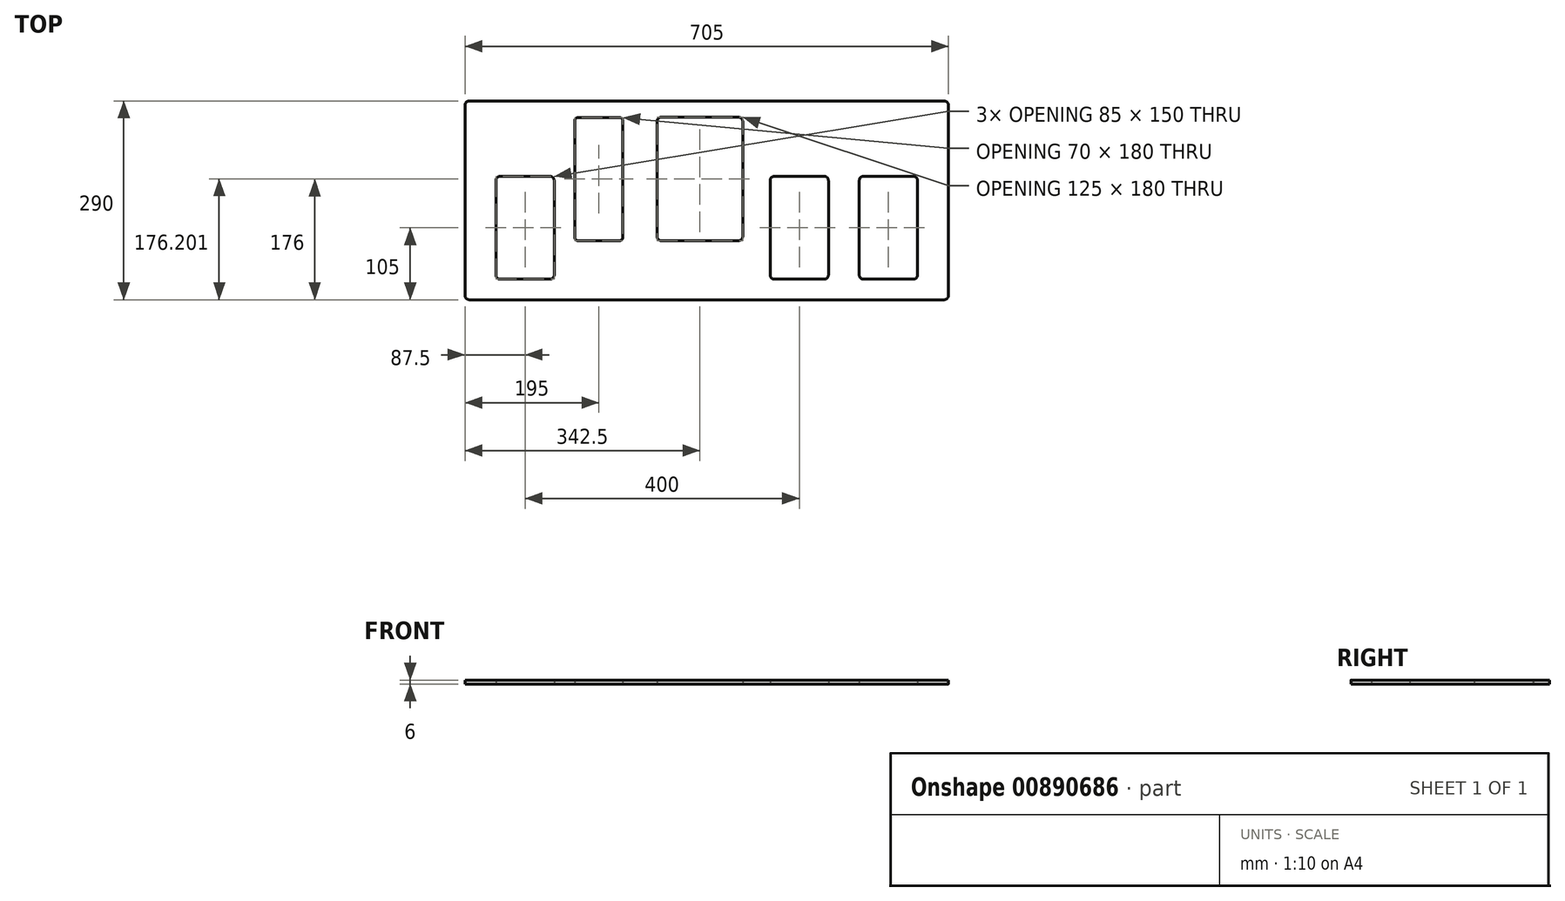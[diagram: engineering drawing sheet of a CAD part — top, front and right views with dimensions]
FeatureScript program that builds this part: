
annotation { "Feature Type Name" : "Feature", "Feature Type Description" : "" }
export const myFeature = defineFeature(function(context is Context, id is Id, definition is map)
    precondition{}
    {
        {
            var Q0;
            Q0=qCreatedBy(makeId("Top.planeOp"),FACE);
            var sketch = newSketch(context, id + "F0", { "sketchPlane" : qUnion([Q0])});
            skLineSegment(sketch, "E0", {"start": v(0, 6) * mm, "end": v(0, 284) * mm});
            skLineSegment(sketch, "E1", {"start": v(6, 290) * mm, "end": v(699, 290) * mm});
            skLineSegment(sketch, "E2", {"start": v(705, 284) * mm, "end": v(705, 6) * mm});
            skLineSegment(sketch, "E3", {"start": v(699, 0) * mm, "end": v(6, 0) * mm});
            skLineSegment(sketch, "E4.bottom", {"start": v(165, 266) * mm, "end": v(225, 266) * mm});
            skLineSegment(sketch, "E4.top", {"start": v(165, 86) * mm, "end": v(225, 86) * mm});
            skLineSegment(sketch, "E4.left", {"start": v(160, 261) * mm, "end": v(160, 91) * mm});
            skLineSegment(sketch, "E4.right", {"start": v(230, 261) * mm, "end": v(230, 91) * mm});
            skPoint(sketch, "E5.visualSharp", {"position": v(230, 266) * mm});
            skArc(sketch, "E5.filletArc", {"start": v(230, 261) * mm, "mid": v(228.54, 264.54) * mm, "end": v(225, 266) * mm});
            skPoint(sketch, "E6.visualSharp", {"position": v(160, 266) * mm});
            skArc(sketch, "E6.filletArc", {"start": v(165, 266) * mm, "mid": v(161.46, 264.54) * mm, "end": v(160, 261) * mm});
            skPoint(sketch, "E7.visualSharp", {"position": v(160, 86) * mm});
            skArc(sketch, "E7.filletArc", {"start": v(160, 91) * mm, "mid": v(161.46, 87.46) * mm, "end": v(165, 86) * mm});
            skPoint(sketch, "E8.visualSharp", {"position": v(230, 86) * mm});
            skArc(sketch, "E8.filletArc", {"start": v(225, 86) * mm, "mid": v(228.54, 87.46) * mm, "end": v(230, 91) * mm});
            skLineSegment(sketch, "E9.bottom", {"start": v(286, 266.2) * mm, "end": v(399, 266.2) * mm});
            skLineSegment(sketch, "E9.top", {"start": v(286, 86.2) * mm, "end": v(399, 86.2) * mm});
            skLineSegment(sketch, "E9.left", {"start": v(280, 260.2) * mm, "end": v(280, 92.2) * mm});
            skLineSegment(sketch, "E9.right", {"start": v(405, 260.2) * mm, "end": v(405, 92.2) * mm});
            skPoint(sketch, "E10.visualSharp", {"position": v(405, 266.2) * mm});
            skArc(sketch, "E10.filletArc", {"start": v(405, 260.2) * mm, "mid": v(403.24, 264.44) * mm, "end": v(399, 266.2) * mm});
            skPoint(sketch, "E11.visualSharp", {"position": v(280, 266.2) * mm});
            skArc(sketch, "E11.filletArc", {"start": v(286, 266.2) * mm, "mid": v(281.76, 264.44) * mm, "end": v(280, 260.2) * mm});
            skPoint(sketch, "E12.visualSharp", {"position": v(280, 86.2) * mm});
            skArc(sketch, "E12.filletArc", {"start": v(280, 92.2) * mm, "mid": v(281.76, 87.96) * mm, "end": v(286, 86.2) * mm});
            skPoint(sketch, "E13.visualSharp", {"position": v(405, 86.2) * mm});
            skArc(sketch, "E13.filletArc", {"start": v(399, 86.2) * mm, "mid": v(403.24, 87.96) * mm, "end": v(405, 92.2) * mm});
            skLineSegment(sketch, "E14.left", {"start": v(130, 36) * mm, "end": v(130, 101.5) * mm});
            skLineSegment(sketch, "E15.bottom", {"start": v(124, 30) * mm, "end": v(51, 30) * mm});
            skLineSegment(sketch, "E15.top", {"start": v(124, 180) * mm, "end": v(51, 180) * mm});
            skLineSegment(sketch, "E15.left", {"start": v(130, 30) * mm, "end": v(130, 174) * mm});
            skLineSegment(sketch, "E15.right", {"start": v(45, 36) * mm, "end": v(45, 174) * mm});
            skPoint(sketch, "E16.visualSharp", {"position": v(130, 180) * mm});
            skArc(sketch, "E16.filletArc", {"start": v(130, 174) * mm, "mid": v(128.24, 178.24) * mm, "end": v(124, 180) * mm});
            skPoint(sketch, "E17.visualSharp", {"position": v(45, 180) * mm});
            skArc(sketch, "E17.filletArc", {"start": v(51, 180) * mm, "mid": v(46.76, 178.24) * mm, "end": v(45, 174) * mm});
            skPoint(sketch, "E18.visualSharp", {"position": v(45, 30) * mm});
            skArc(sketch, "E18.filletArc", {"start": v(45, 36) * mm, "mid": v(46.76, 31.76) * mm, "end": v(51, 30) * mm});
            skPoint(sketch, "E19.visualSharp", {"position": v(130, 30) * mm});
            skArc(sketch, "E19.filletArc", {"start": v(124, 30) * mm, "mid": v(128.24, 31.76) * mm, "end": v(130, 36) * mm});
            skLineSegment(sketch, "E20.bottom", {"start": v(451, 180) * mm, "end": v(524, 180) * mm});
            skLineSegment(sketch, "E20.top", {"start": v(451, 30) * mm, "end": v(524, 30) * mm});
            skLineSegment(sketch, "E20.left", {"start": v(445, 174) * mm, "end": v(445, 36) * mm});
            skLineSegment(sketch, "E20.right", {"start": v(530, 174) * mm, "end": v(530, 36) * mm});
            skPoint(sketch, "E21.visualSharp", {"position": v(530, 180) * mm});
            skArc(sketch, "E21.filletArc", {"start": v(530, 174) * mm, "mid": v(528.24, 178.24) * mm, "end": v(524, 180) * mm});
            skPoint(sketch, "E22.visualSharp", {"position": v(445, 180) * mm});
            skArc(sketch, "E22.filletArc", {"start": v(451, 180) * mm, "mid": v(446.76, 178.24) * mm, "end": v(445, 174) * mm});
            skPoint(sketch, "E23.visualSharp", {"position": v(445, 30) * mm});
            skArc(sketch, "E23.filletArc", {"start": v(445, 36) * mm, "mid": v(446.76, 31.76) * mm, "end": v(451, 30) * mm});
            skPoint(sketch, "E24.visualSharp", {"position": v(530, 30) * mm});
            skArc(sketch, "E24.filletArc", {"start": v(524, 30) * mm, "mid": v(528.24, 31.76) * mm, "end": v(530, 36) * mm});
            skLineSegment(sketch, "E25.bottom", {"start": v(581, 180) * mm, "end": v(654, 180) * mm});
            skLineSegment(sketch, "E25.top", {"start": v(581, 30) * mm, "end": v(654, 30) * mm});
            skLineSegment(sketch, "E25.left", {"start": v(575, 174) * mm, "end": v(575, 36) * mm});
            skLineSegment(sketch, "E25.right", {"start": v(660, 174) * mm, "end": v(660, 36) * mm});
            skPoint(sketch, "E26.visualSharp", {"position": v(660, 180) * mm});
            skArc(sketch, "E26.filletArc", {"start": v(660, 174) * mm, "mid": v(658.24, 178.24) * mm, "end": v(654, 180) * mm});
            skPoint(sketch, "E27.visualSharp", {"position": v(575, 180) * mm});
            skArc(sketch, "E27.filletArc", {"start": v(581, 180) * mm, "mid": v(576.76, 178.24) * mm, "end": v(575, 174) * mm});
            skPoint(sketch, "E28.visualSharp", {"position": v(575, 30) * mm});
            skArc(sketch, "E28.filletArc", {"start": v(575, 36) * mm, "mid": v(576.76, 31.76) * mm, "end": v(581, 30) * mm});
            skPoint(sketch, "E29.visualSharp", {"position": v(660, 30) * mm});
            skArc(sketch, "E29.filletArc", {"start": v(654, 30) * mm, "mid": v(658.24, 31.76) * mm, "end": v(660, 36) * mm});
            skPoint(sketch, "E30.visualSharp", {"position": v(705, 290) * mm});
            skArc(sketch, "E30.filletArc", {"start": v(705, 284) * mm, "mid": v(703.24, 288.24) * mm, "end": v(699, 290) * mm});
            skPoint(sketch, "E31.visualSharp", {"position": v(0, 290) * mm});
            skArc(sketch, "E31.filletArc", {"start": v(6, 290) * mm, "mid": v(1.76, 288.24) * mm, "end": v(0, 284) * mm});
            skPoint(sketch, "E32.visualSharp", {"position": v(0, 0) * mm});
            skArc(sketch, "E32.filletArc", {"start": v(0, 6) * mm, "mid": v(1.76, 1.76) * mm, "end": v(6, 0) * mm});
            skPoint(sketch, "E33.visualSharp", {"position": v(705, 0) * mm});
            skArc(sketch, "E33.filletArc", {"start": v(699, 0) * mm, "mid": v(703.24, 1.76) * mm, "end": v(705, 6) * mm});
            skSolve(sketch);
        }
        {
            var Q0;
            Q0=makeQuery(id+"F0.imprint","IMPRINT",FACE,{"disambiguationData":[TD([[makeQuery(id+"F0.imprint","IMPRINT",EDGE,{"derivedFrom":sQuery(id+"F0.wireOp",EDGE,"E0")}),-1.0]])]});
            extrude(context, id + "F1", {"entities" : qUnion([Q0]), "depth" : 6 * mm, "offsetDistance" : 25 * mm});
        }
    });
